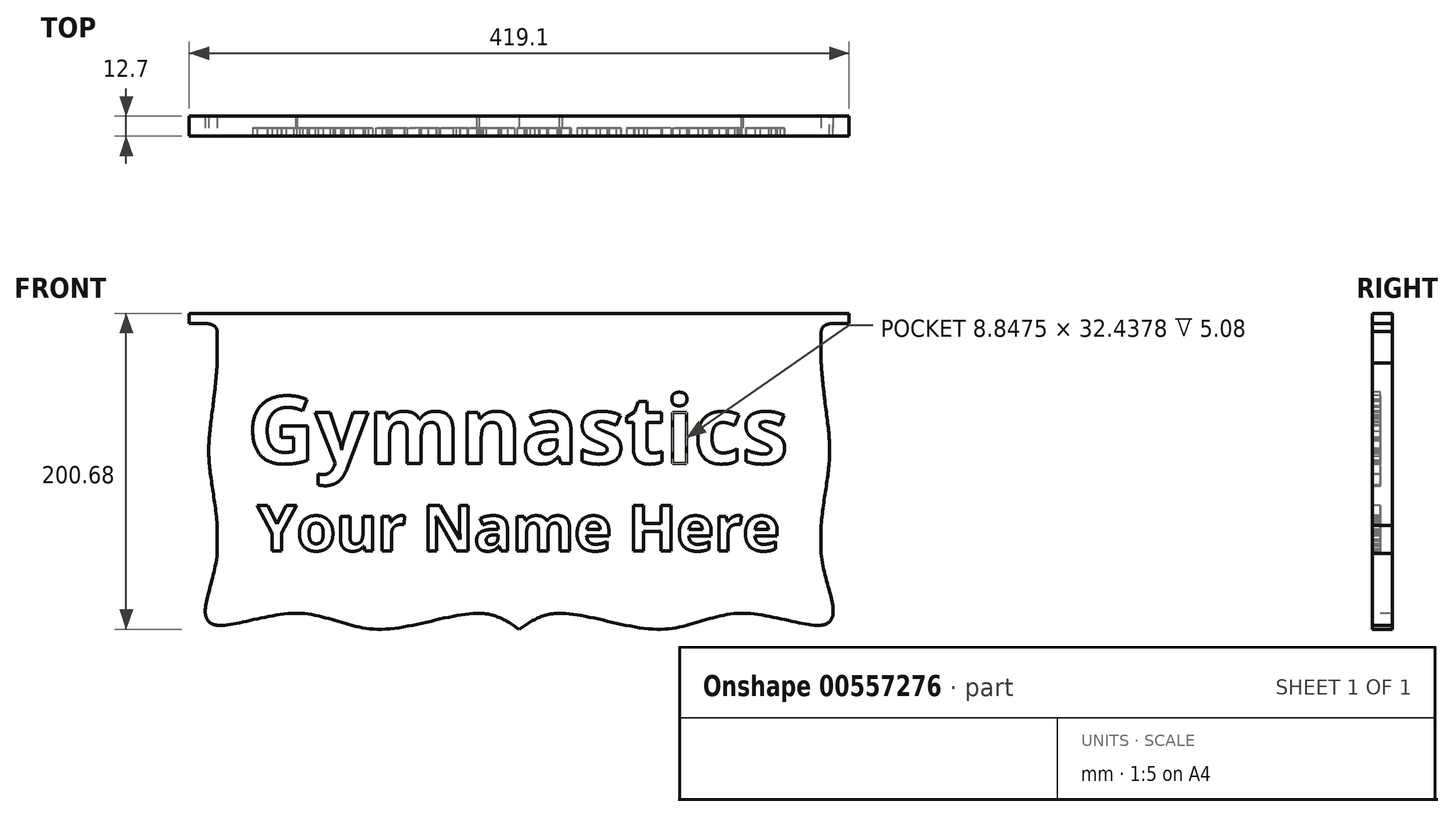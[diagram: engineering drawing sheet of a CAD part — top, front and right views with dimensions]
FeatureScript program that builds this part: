
annotation { "Feature Type Name" : "Feature", "Feature Type Description" : "" }
export const myFeature = defineFeature(function(context is Context, id is Id, definition is map)
    precondition{}
    {
        {
            var Q0;
            Q0=qCreatedBy(makeId("Front.planeOp"),FACE);
            var sketch = newSketch(context, id + "F0", { "sketchPlane" : qUnion([Q0])});
            skLineSegment(sketch, "E0.bottom", {"start": v(-209.55, 95.25) * mm, "end": v(209.55, 95.25) * mm});
            skLineSegment(sketch, "E0.top", {"start": v(-209.55, -95.25) * mm, "end": v(209.55, -95.25) * mm});
            skLineSegment(sketch, "E0.left", {"start": v(-209.55, 95.25) * mm, "end": v(-209.55, -95.25) * mm});
            skLineSegment(sketch, "E0.right", {"start": v(209.55, 95.25) * mm, "end": v(209.55, -95.25) * mm});
            skPoint(sketch, "E0.middle", {"position": v(0, 0) * mm});
            skSolve(sketch);
        }
        {
            var Q0;
            Q0=makeQuery(id+"F0.imprint","IMPRINT",FACE,{"disambiguationData":[TD([[makeQuery(id+"F0.imprint","IMPRINT",EDGE,{"derivedFrom":sQuery(id+"F0.wireOp",EDGE,"E0.bottom")}),-1.0]])]});
            extrude(context, id + "F1", {"entities" : qUnion([Q0]), "depth" : 12.7 * mm});
        }
        {
            var Q0;
            Q0=makeQuery(id+"F1.opExtrude","CAP_FACE",FACE,{"disambiguationData":[OSD([sQuery(id+"F0.wireOp",EDGE,"E0.bottom"),sQuery(id+"F0.wireOp",EDGE,"E0.top"),sQuery(id+"F0.wireOp",EDGE,"E0.left"),sQuery(id+"F0.wireOp",EDGE,"E0.right")])],"isStart":false});
            var sketch = newSketch(context, id + "F2", { "sketchPlane" : qUnion([Q0])});
            skText(sketch, "E1", { "text": "Gymnastics", "fontName": "OpenSans-Bold.ttf"});
            skText(sketch, "E2", { "text": "Your Name Here", "fontName": "OpenSans-Bold.ttf"});
            const initialGuessF2  = {"E1": [-0.17278, 0, 1, 0, 0.04278], "E2": [-0.16647, -0.05555, 1, 0, 0.02893]};
            skSetInitialGuess(sketch, initialGuessF2);
            skSolve(sketch);
        }
        {
            var Q0;
            Q0=qSketchRegion(id+"F2",true);
            extrude(context, id + "F3", {"entities" : qUnion([Q0]), "operationType" : NewBodyOperationType.REMOVE, "oppositeDirection" : true, "depth" : 5.08 * mm});
        }
        {
            var Q0;
            {var subQ0=sQuery(id+"F0.wireOp",EDGE,"E0.left");var subQ1=sQuery(id+"F0.wireOp",EDGE,"E0.bottom");var subQ2=sQuery(id+"F0.wireOp",EDGE,"E0.right");var subQ3=sQuery(id+"F0.wireOp",EDGE,"E0.top");Q0=makeQuery(id+"F3.boolean.opBoolean","SPLIT",FACE,{"disambiguationData":[TD([makeQuery(id+"F1.opExtrude","SWEPT_FACE",FACE,{"disambiguationData":[OSD([subQ1])]})])],"derivedFrom":makeQuery(id+"F1.opExtrude","CAP_FACE",FACE,{"disambiguationData":[OSD([subQ1,subQ3,subQ0,subQ2])],"isStart":false})});}
            var sketch = newSketch(context, id + "F4", { "sketchPlane" : qUnion([Q0])});
            skPoint(sketch, "E3", {"position": v(-191.77, 95.25) * mm});
            skPoint(sketch, "E4", {"position": v(-191.77, -95.25) * mm});
            skPoint(sketch, "E5", {"position": v(191.77, 95.25) * mm});
            skPoint(sketch, "E6", {"position": v(209.55, 88.9) * mm});
            skPoint(sketch, "E7", {"position": v(191.77, -95.25) * mm});
            skPoint(sketch, "E8", {"position": v(-209.55, 88.9) * mm});
            skLineSegment(sketch, "E9", {"start": v(-191.77, 95.25) * mm, "end": v(-191.77, -95.25) * mm});
            skLineSegment(sketch, "E10", {"start": v(-209.55, 88.9) * mm, "end": v(-191.77, 88.9) * mm});
            skLineSegment(sketch, "E11", {"start": v(191.77, -95.25) * mm, "end": v(191.77, 95.25) * mm});
            skLineSegment(sketch, "E12", {"start": v(209.55, 88.9) * mm, "end": v(191.77, 88.9) * mm});
            skPoint(sketch, "E13", {"position": v(-32.37, -40.44) * mm});
            skPoint(sketch, "E14", {"position": v(-37.84, -40.44) * mm});
            skSolve(sketch);
        }
        {
            var Q0;
            {var subQ3=sQuery(id+"F4.wireOp",EDGE,"E10");Q0=makeQuery(id+"F4.imprint","IMPRINT",FACE,{"disambiguationData":[TD([[makeQuery(id+"F4.imprint","IMPRINT",EDGE,{"derivedFrom":subQ3}),-1.0]])]});}
            var Q1;
            {var subQ3=sQuery(id+"F4.wireOp",EDGE,"E12");Q1=makeQuery(id+"F4.imprint","IMPRINT",FACE,{"disambiguationData":[TD([[makeQuery(id+"F4.imprint","IMPRINT",EDGE,{"derivedFrom":subQ3}),1.0]])]});}
            extrude(context, id + "F5", {"entities" : qUnion([Q0, Q1]), "operationType" : NewBodyOperationType.REMOVE, "oppositeDirection" : true, "depth" : 12.7 * mm});
        }
        {
            var Q0;
            {var subQ0=sQuery(id+"F0.wireOp",EDGE,"E0.left");var subQ1=sQuery(id+"F0.wireOp",EDGE,"E0.bottom");var subQ2=sQuery(id+"F0.wireOp",EDGE,"E0.right");var subQ3=sQuery(id+"F0.wireOp",EDGE,"E0.top");Q0=makeQuery(id+"F3.boolean.opBoolean","SPLIT",FACE,{"disambiguationData":[TD([makeQuery(id+"F1.opExtrude","SWEPT_FACE",FACE,{"disambiguationData":[OSD([subQ1])]})])],"derivedFrom":makeQuery(id+"F1.opExtrude","CAP_FACE",FACE,{"disambiguationData":[OSD([subQ1,subQ3,subQ0,subQ2])],"isStart":false})});}
            var sketch = newSketch(context, id + "F6", { "sketchPlane" : qUnion([Q0])});
            skPoint(sketch, "E15", {"position": v(-191.77, 38.1) * mm});
            skPoint(sketch, "E16", {"position": v(-191.77, 0) * mm});
            skPoint(sketch, "E17", {"position": v(-191.77, -57.15) * mm});
            skPoint(sketch, "E18", {"position": v(-140.97, -95.25) * mm});
            skPoint(sketch, "E19", {"position": v(-90.17, -95.25) * mm});
            skPoint(sketch, "E20", {"position": v(0, -95.25) * mm});
            skPoint(sketch, "E21", {"position": v(90.17, -95.25) * mm});
            skPoint(sketch, "E22", {"position": v(140.97, -95.25) * mm});
            skPoint(sketch, "E23", {"position": v(191.77, -57.15) * mm});
            skPoint(sketch, "E24", {"position": v(191.77, 0) * mm});
            skPoint(sketch, "E25", {"position": v(191.77, 38.1) * mm});
            skLineSegment(sketch, "E26", {"start": v(-191.77, 0) * mm, "end": v(-196.85, 0) * mm});
            skLineSegment(sketch, "E27", {"start": v(-191.77, 38.1) * mm, "end": v(-194.3, 38.1) * mm});
            skLineSegment(sketch, "E28", {"start": v(-191.77, -95.25) * mm, "end": v(-199.39, -95.25) * mm});
            skLineSegment(sketch, "E29", {"start": v(-191.77, -95.25) * mm, "end": v(-191.77, -102.87) * mm});
            skLineSegment(sketch, "E30", {"start": v(-90.17, -95.25) * mm, "end": v(-90.17, -105.41) * mm});
            skLineSegment(sketch, "E31", {"start": v(191.77, 38.1) * mm, "end": v(194.31, 38.1) * mm});
            skLineSegment(sketch, "E32", {"start": v(191.77, 0) * mm, "end": v(196.85, 0) * mm});
            skLineSegment(sketch, "E33", {"start": v(191.77, -95.25) * mm, "end": v(199.4, -95.25) * mm});
            skLineSegment(sketch, "E34", {"start": v(191.77, -95.25) * mm, "end": v(191.77, -102.87) * mm});
            skLineSegment(sketch, "E35", {"start": v(90.17, -95.25) * mm, "end": v(90.17, -105.41) * mm});
            skPoint(sketch, "E36", {"position": v(25.4, -95.25) * mm});
            skPoint(sketch, "E37", {"position": v(-25.4, -95.25) * mm});
            skLineSegment(sketch, "E38", {"start": v(0, -95.25) * mm, "end": v(0, -105.41) * mm});
            skPoint(sketch, "E39", {"position": v(199.4, 88.9) * mm});
            skPoint(sketch, "E40", {"position": v(191.77, 83.82) * mm});
            skPoint(sketch, "E41", {"position": v(194.31, 88.9) * mm});
            skLineSegment(sketch, "E42", {"start": v(194.31, 88.9) * mm, "end": v(194.31, 87.63) * mm});
            skFitSpline(sketch, "E43", {"points": [v(0, -105.41) * mm, v(25.4, -95.25) * mm, v(90.17, -105.41) * mm, v(140.97, -95.25) * mm, v(191.77, -102.87) * mm, v(199.4, -95.25) * mm, v(191.77, -57.15) * mm, v(196.85, 0) * mm, v(194.31, 38.1) * mm, v(191.77, 83.82) * mm, v(194.31, 87.63) * mm, v(199.4, 88.9) * mm], "startDerivative": vector(254.46, 176.78) * mm, "endDerivative": vector(162.96, 9.49) * mm});
            skPoint(sketch, "E44", {"position": v(-199.39, 88.9) * mm});
            skPoint(sketch, "E45", {"position": v(-191.77, 83.82) * mm});
            skPoint(sketch, "E46", {"position": v(-194.3, 88.9) * mm});
            skLineSegment(sketch, "E47", {"start": v(-194.3, 88.9) * mm, "end": v(-194.3, 87.63) * mm});
            skFitSpline(sketch, "E48", {"points": [v(0, -105.41) * mm, v(-25.4, -95.25) * mm, v(-90.17, -105.41) * mm, v(-140.97, -95.25) * mm, v(-191.77, -102.87) * mm, v(-199.39, -95.25) * mm, v(-191.77, -57.15) * mm, v(-196.85, 0) * mm, v(-194.3, 38.1) * mm, v(-191.77, 83.82) * mm, v(-194.3, 87.63) * mm, v(-199.39, 88.9) * mm], "startDerivative": vector(-252.39, 175.34) * mm, "endDerivative": vector(-141.61, 8.53) * mm});
            skSolve(sketch);
        }
        {
            var Q0;
            Q0 = qSketchRegion(id + "F6", true);
            var Q1;
            {var subQ0=sQuery(id+"F6.wireOp",EDGE,"9e0a6239-fdb5-4647-a296-c43551efd45f");var subQ1=makeQuery(id+"F5.boolean.opBoolean","COPY",EDGE,{"derivedFrom":makeQuery(id+"F5.opExtrude","CAP_EDGE",EDGE,{"disambiguationData":[OSD([sQuery(id+"F4.wireOp",EDGE,"E11")])],"isStart":true})});var subQ2=makeQuery(id+"F6.imprint","INTERSECT",VERTEX,{"disambiguationData":[OD(0.0)],"derivedFrom":[subQ1,subQ0]});Q1=makeQuery(id+"F6.imprint","IMPRINT",FACE,{"disambiguationData":[TD([[makeQuery(id+"F6.imprint","IMPRINT",EDGE,{"disambiguationData":[TD([[subQ2,-1.0]])],"derivedFrom":subQ0}),1.0]])]});}
            var Q2;
            {var subQ0=sQuery(id+"F6.wireOp",EDGE,"d2f81a62-16b6-484c-80cf-df5878542265");var subQ1=makeQuery(id+"F5.boolean.opBoolean","COPY",EDGE,{"derivedFrom":makeQuery(id+"F5.opExtrude","CAP_EDGE",EDGE,{"disambiguationData":[OSD([sQuery(id+"F4.wireOp",EDGE,"E9")])],"isStart":true})});var subQ2=makeQuery(id+"F6.imprint","INTERSECT",VERTEX,{"disambiguationData":[OD(0.0)],"derivedFrom":[subQ1,subQ0]});Q2=makeQuery(id+"F6.imprint","IMPRINT",FACE,{"disambiguationData":[TD([[makeQuery(id+"F6.imprint","IMPRINT",EDGE,{"disambiguationData":[TD([[subQ2,-1.0]])],"derivedFrom":subQ0}),-1.0]])]});}
            var Q3;
            {var subQ0=sQuery(id+"F6.wireOp",EDGE,"E43");var subQ1=makeQuery(id+"F5.boolean.opBoolean","COPY",EDGE,{"derivedFrom":makeQuery(id+"F5.opExtrude","CAP_EDGE",EDGE,{"disambiguationData":[OSD([sQuery(id+"F4.wireOp",EDGE,"E11")])],"isStart":true})});var subQ2=makeQuery(id+"F6.imprint","INTERSECT",VERTEX,{"disambiguationData":[OD(2.0)],"derivedFrom":[subQ1,subQ0]});Q3=makeQuery(id+"F6.imprint","IMPRINT",FACE,{"disambiguationData":[TD([[makeQuery(id+"F6.imprint","IMPRINT",EDGE,{"disambiguationData":[TD([[subQ2,-1.0]])],"derivedFrom":subQ0}),-1.0]])]});}
            var Q4;
            {var subQ0=sQuery(id+"F6.wireOp",EDGE,"E48");var subQ1=makeQuery(id+"F5.boolean.opBoolean","COPY",EDGE,{"derivedFrom":makeQuery(id+"F5.opExtrude","CAP_EDGE",EDGE,{"disambiguationData":[OSD([sQuery(id+"F4.wireOp",EDGE,"E9")])],"isStart":true})});var subQ2=makeQuery(id+"F6.imprint","INTERSECT",VERTEX,{"disambiguationData":[OD(2.0)],"derivedFrom":[subQ1,subQ0]});Q4=makeQuery(id+"F6.imprint","IMPRINT",FACE,{"disambiguationData":[TD([[makeQuery(id+"F6.imprint","IMPRINT",EDGE,{"disambiguationData":[TD([[subQ2,-1.0]])],"derivedFrom":subQ0}),1.0]])]});}
            var Q5;
            {var subQ0=sQuery(id+"F6.wireOp",EDGE,"E48");var subQ1=makeQuery(id+"F5.boolean.opBoolean","COPY",EDGE,{"derivedFrom":makeQuery(id+"F5.opExtrude","CAP_EDGE",EDGE,{"disambiguationData":[OSD([sQuery(id+"F4.wireOp",EDGE,"E9")])],"isStart":true})});var subQ2=makeQuery(id+"F6.imprint","INTERSECT",VERTEX,{"disambiguationData":[OD(0.0)],"derivedFrom":[subQ1,subQ0]});Q5=makeQuery(id+"F6.imprint","IMPRINT",FACE,{"disambiguationData":[TD([[makeQuery(id+"F6.imprint","IMPRINT",EDGE,{"disambiguationData":[TD([[subQ2,-1.0]])],"derivedFrom":subQ0}),1.0]])]});}
            var Q6;
            {var subQ0=sQuery(id+"F6.wireOp",EDGE,"E43");var subQ1=makeQuery(id+"F5.boolean.opBoolean","COPY",EDGE,{"derivedFrom":makeQuery(id+"F5.opExtrude","CAP_EDGE",EDGE,{"disambiguationData":[OSD([sQuery(id+"F4.wireOp",EDGE,"E11")])],"isStart":true})});var subQ2=makeQuery(id+"F6.imprint","INTERSECT",VERTEX,{"disambiguationData":[OD(0.0)],"derivedFrom":[subQ1,subQ0]});Q6=makeQuery(id+"F6.imprint","IMPRINT",FACE,{"disambiguationData":[TD([[makeQuery(id+"F6.imprint","IMPRINT",EDGE,{"disambiguationData":[TD([[subQ2,-1.0]])],"derivedFrom":subQ0}),-1.0]])]});}
            extrude(context, id + "F7", {"entities" : qUnion([Q0, Q1, Q2, Q3, Q4, Q5, Q6]), "operationType" : NewBodyOperationType.REMOVE, "oppositeDirection" : true, "depth" : 12.7 * mm, "offsetDistance" : 25.4 * mm});
        }
        {
            var Q0;
            {var subQ0=sQuery(id+"F6.wireOp",EDGE,"E26");Q0=makeQuery(id+"F6.imprint","IMPRINT",FACE,{"disambiguationData":[TD([[makeQuery(id+"F6.imprint","IMPRINT",EDGE,{"derivedFrom":subQ0}),-1.0]])]});}
            var Q1;
            {var subQ0=sQuery(id+"F6.wireOp",EDGE,"E26");Q1=makeQuery(id+"F6.imprint","IMPRINT",FACE,{"disambiguationData":[TD([[makeQuery(id+"F6.imprint","IMPRINT",EDGE,{"derivedFrom":subQ0}),1.0]])]});}
            var Q2;
            {var subQ0=sQuery(id+"F6.wireOp",EDGE,"E27");Q2=makeQuery(id+"F6.imprint","IMPRINT",FACE,{"disambiguationData":[TD([[makeQuery(id+"F6.imprint","IMPRINT",EDGE,{"derivedFrom":subQ0}),-1.0]])]});}
            var Q3;
            {var subQ0=sQuery(id+"F6.wireOp",EDGE,"E28");Q3=makeQuery(id+"F6.imprint","IMPRINT",FACE,{"disambiguationData":[TD([[makeQuery(id+"F6.imprint","IMPRINT",EDGE,{"derivedFrom":subQ0}),-1.0]])]});}
            var Q4;
            {var subQ0=sQuery(id+"F6.wireOp",EDGE,"E28");Q4=makeQuery(id+"F6.imprint","IMPRINT",FACE,{"disambiguationData":[TD([[makeQuery(id+"F6.imprint","IMPRINT",EDGE,{"derivedFrom":subQ0}),1.0]])]});}
            var Q5;
            {var subQ0=sQuery(id+"F6.wireOp",EDGE,"E29");Q5=makeQuery(id+"F6.imprint","IMPRINT",FACE,{"disambiguationData":[TD([[makeQuery(id+"F6.imprint","IMPRINT",EDGE,{"derivedFrom":subQ0}),1.0]])]});}
            var Q6;
            {var subQ0=sQuery(id+"F6.wireOp",EDGE,"E30");Q6=makeQuery(id+"F6.imprint","IMPRINT",FACE,{"disambiguationData":[TD([[makeQuery(id+"F6.imprint","IMPRINT",EDGE,{"derivedFrom":subQ0}),-1.0]])]});}
            var Q7;
            {var subQ0=sQuery(id+"F6.wireOp",EDGE,"E30");Q7=makeQuery(id+"F6.imprint","IMPRINT",FACE,{"disambiguationData":[TD([[makeQuery(id+"F6.imprint","IMPRINT",EDGE,{"derivedFrom":subQ0}),1.0]])]});}
            var Q8;
            {var subQ0=sQuery(id+"F6.wireOp",EDGE,"E38");Q8=makeQuery(id+"F6.imprint","IMPRINT",FACE,{"disambiguationData":[TD([[makeQuery(id+"F6.imprint","IMPRINT",EDGE,{"derivedFrom":subQ0}),-1.0]])]});}
            var Q9;
            {var subQ0=sQuery(id+"F6.wireOp",EDGE,"E38");Q9=makeQuery(id+"F6.imprint","IMPRINT",FACE,{"disambiguationData":[TD([[makeQuery(id+"F6.imprint","IMPRINT",EDGE,{"derivedFrom":subQ0}),1.0]])]});}
            var Q10;
            {var subQ0=sQuery(id+"F6.wireOp",EDGE,"9e0a6239-fdb5-4647-a296-c43551efd45f");var subQ1=sQuery(id+"F6.wireOp",EDGE,"E35");var subQ2=makeQuery(id+"F6.imprint","INTERSECT",VERTEX,{"derivedFrom":[subQ1,subQ0]});Q10=makeQuery(id+"F6.imprint","IMPRINT",FACE,{"disambiguationData":[TD([[makeQuery(id+"F6.imprint","IMPRINT",EDGE,{"disambiguationData":[TD([[subQ2,1.0]])],"derivedFrom":subQ1}),-1.0]])]});}
            var Q11;
            {var subQ0=sQuery(id+"F6.wireOp",EDGE,"9e0a6239-fdb5-4647-a296-c43551efd45f");var subQ1=sQuery(id+"F6.wireOp",EDGE,"E35");var subQ2=makeQuery(id+"F6.imprint","INTERSECT",VERTEX,{"derivedFrom":[subQ1,subQ0]});Q11=makeQuery(id+"F6.imprint","IMPRINT",FACE,{"disambiguationData":[TD([[makeQuery(id+"F6.imprint","IMPRINT",EDGE,{"disambiguationData":[TD([[subQ2,1.0]])],"derivedFrom":subQ1}),1.0]])]});}
            var Q12;
            {var subQ0=sQuery(id+"F6.wireOp",EDGE,"E34");Q12=makeQuery(id+"F6.imprint","IMPRINT",FACE,{"disambiguationData":[TD([[makeQuery(id+"F6.imprint","IMPRINT",EDGE,{"derivedFrom":subQ0}),-1.0]])]});}
            var Q13;
            {var subQ0=sQuery(id+"F6.wireOp",EDGE,"E33");Q13=makeQuery(id+"F6.imprint","IMPRINT",FACE,{"disambiguationData":[TD([[makeQuery(id+"F6.imprint","IMPRINT",EDGE,{"derivedFrom":subQ0}),-1.0]])]});}
            var Q14;
            {var subQ0=sQuery(id+"F6.wireOp",EDGE,"E33");Q14=makeQuery(id+"F6.imprint","IMPRINT",FACE,{"disambiguationData":[TD([[makeQuery(id+"F6.imprint","IMPRINT",EDGE,{"derivedFrom":subQ0}),1.0]])]});}
            var Q15;
            {var subQ0=sQuery(id+"F6.wireOp",EDGE,"E32");Q15=makeQuery(id+"F6.imprint","IMPRINT",FACE,{"disambiguationData":[TD([[makeQuery(id+"F6.imprint","IMPRINT",EDGE,{"derivedFrom":subQ0}),-1.0]])]});}
            var Q16;
            {var subQ0=sQuery(id+"F6.wireOp",EDGE,"E31");Q16=makeQuery(id+"F6.imprint","IMPRINT",FACE,{"disambiguationData":[TD([[makeQuery(id+"F6.imprint","IMPRINT",EDGE,{"derivedFrom":subQ0}),-1.0]])]});}
            var Q17;
            {var subQ0=sQuery(id+"F6.wireOp",EDGE,"E31");Q17=makeQuery(id+"F6.imprint","IMPRINT",FACE,{"disambiguationData":[TD([[makeQuery(id+"F6.imprint","IMPRINT",EDGE,{"derivedFrom":subQ0}),1.0]])]});}
            var Q18;
            {var subQ0=sQuery(id+"F6.wireOp",EDGE,"9e0a6239-fdb5-4647-a296-c43551efd45f");var subQ1=makeQuery(id+"F6.imprint","IMPRINT",VERTEX,{"derivedFrom":subQ0});Q18=makeQuery(id+"F6.imprint","IMPRINT",FACE,{"disambiguationData":[TD([[makeQuery(id+"F6.imprint","IMPRINT",EDGE,{"disambiguationData":[TD([[subQ1,1.0]])],"derivedFrom":subQ0}),-1.0]])]});}
            var Q19;
            {var subQ0=sQuery(id+"F6.wireOp",EDGE,"E42");Q19=makeQuery(id+"F6.imprint","IMPRINT",FACE,{"disambiguationData":[TD([[makeQuery(id+"F6.imprint","IMPRINT",EDGE,{"derivedFrom":subQ0}),-1.0]])]});}
            var Q20;
            {var subQ0=sQuery(id+"F6.wireOp",EDGE,"E42");Q20=makeQuery(id+"F6.imprint","IMPRINT",FACE,{"disambiguationData":[TD([[makeQuery(id+"F6.imprint","IMPRINT",EDGE,{"derivedFrom":subQ0}),1.0]])]});}
            var Q21;
            {var subQ0=sQuery(id+"F6.wireOp",EDGE,"E47");Q21=makeQuery(id+"F6.imprint","IMPRINT",FACE,{"disambiguationData":[TD([[makeQuery(id+"F6.imprint","IMPRINT",EDGE,{"derivedFrom":subQ0}),1.0]])]});}
            var Q22;
            {var subQ0=sQuery(id+"F6.wireOp",EDGE,"E47");Q22=makeQuery(id+"F6.imprint","IMPRINT",FACE,{"disambiguationData":[TD([[makeQuery(id+"F6.imprint","IMPRINT",EDGE,{"derivedFrom":subQ0}),-1.0]])]});}
            extrude(context, id + "F8", {"entities" : qUnion([Q0, Q1, Q2, Q3, Q4, Q5, Q6, Q7, Q8, Q9, Q10, Q11, Q12, Q13, Q14, Q15, Q16, Q17, Q18, Q19, Q20, Q21, Q22]), "operationType" : NewBodyOperationType.ADD, "depth" : -12.7 * mm, "offsetDistance" : 25.4 * mm});
        }
    });
